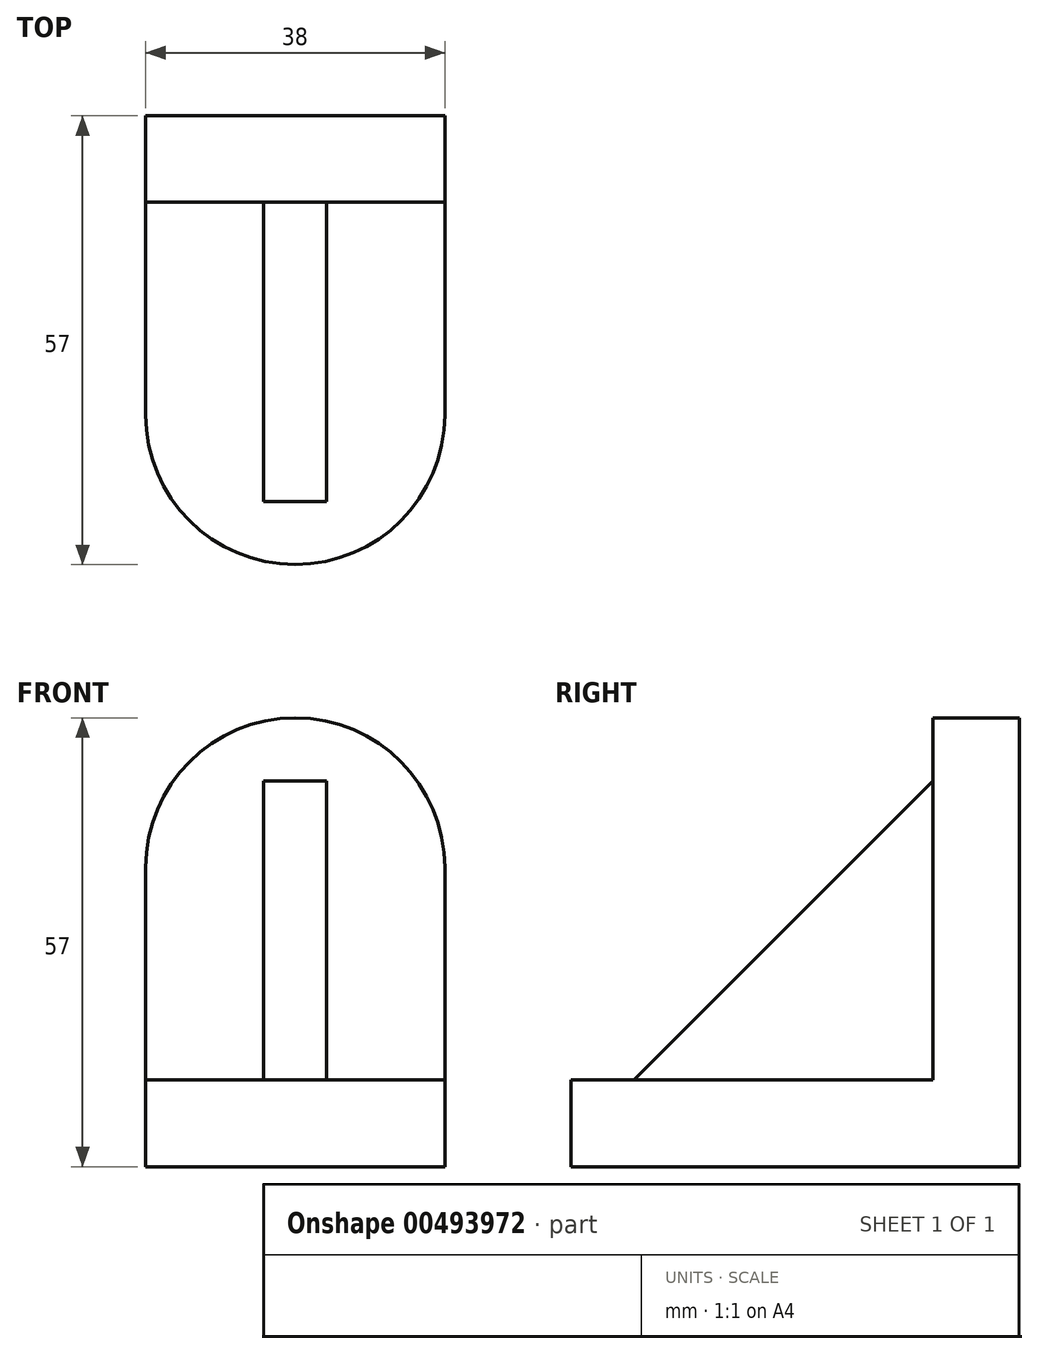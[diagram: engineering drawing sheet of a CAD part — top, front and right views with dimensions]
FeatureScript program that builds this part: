
annotation { "Feature Type Name" : "Feature", "Feature Type Description" : "" }
export const myFeature = defineFeature(function(context is Context, id is Id, definition is map)
    precondition{}
    {
        {
            var Q0;
            Q0=qCreatedBy(makeId("Front.planeOp"),FACE);
            var sketch = newSketch(context, id + "F0", { "sketchPlane" : qUnion([Q0])});
            skLineSegment(sketch, "E0.bottom", {"start": v(-19, 0) * mm, "end": v(19, 0) * mm});
            skLineSegment(sketch, "E0.left", {"start": v(-19, 0) * mm, "end": v(-19, 38) * mm});
            skLineSegment(sketch, "E0.right", {"start": v(19, 0) * mm, "end": v(19, 38) * mm});
            skArc(sketch, "E1", {"start": v(19, 38) * mm, "mid": v(0, 57) * mm, "end": v(-19, 38) * mm});
            skSolve(sketch);
        }
        {
            var Q0;
            Q0=makeQuery(id+"F0.imprint","IMPRINT",FACE,{"disambiguationData":[TD([[makeQuery(id+"F0.imprint","IMPRINT",EDGE,{"derivedFrom":sQuery(id+"F0.wireOp",EDGE,"E0.bottom")}),1.0]])]});
            extrude(context, id + "F1", {"entities" : qUnion([Q0]), "depth" : 11 * mm});
        }
        {
            var Q0;
            Q0=qCreatedBy(makeId("Top.planeOp"),FACE);
            var sketch = newSketch(context, id + "F2", { "sketchPlane" : qUnion([Q0])});
            skLineSegment(sketch, "E2.bottom", {"start": v(-19, 0) * mm, "end": v(19, 0) * mm});
            skLineSegment(sketch, "E2.left", {"start": v(-19, 0) * mm, "end": v(-19, -38) * mm});
            skLineSegment(sketch, "E2.right", {"start": v(19, 0) * mm, "end": v(19, -38) * mm});
            skArc(sketch, "E3", {"start": v(-19, -38) * mm, "mid": v(0, -57) * mm, "end": v(19, -38) * mm});
            skSolve(sketch);
        }
        {
            var Q0;
            Q0=makeQuery(id+"F2.imprint","IMPRINT",FACE,{"disambiguationData":[TD([[makeQuery(id+"F2.imprint","IMPRINT",EDGE,{"derivedFrom":sQuery(id+"F2.wireOp",EDGE,"E2.bottom")}),-1.0]])]});
            extrude(context, id + "F3", {"entities" : qUnion([Q0]), "operationType" : NewBodyOperationType.ADD, "depth" : 11 * mm});
        }
        {
            var Q0;
            Q0=qCreatedBy(makeId("Right.planeOp"),FACE);
            var sketch = newSketch(context, id + "F4", { "sketchPlane" : qUnion([Q0])});
            skLineSegment(sketch, "E4", {"start": v(-49, 11) * mm, "end": v(-11, 49) * mm});
            skLineSegment(sketch, "E5", {"start": v(-11, 49) * mm, "end": v(-11, 9.03) * mm});
            skLineSegment(sketch, "E6", {"start": v(-11, 9.03) * mm, "end": v(-49, 11) * mm});
            skSolve(sketch);
        }
        {
            var Q0;
            Q0=makeQuery(id+"F4.imprint","IMPRINT",FACE,{"disambiguationData":[TD([[makeQuery(id+"F4.imprint","IMPRINT",EDGE,{"derivedFrom":sQuery(id+"F4.wireOp",EDGE,"E4")}),-1.0]])]});
            extrude(context, id + "F5", {"entities" : qUnion([Q0]), "operationType" : NewBodyOperationType.ADD, "depth" : 4 * mm});
        }
        {
            var Q0;
            Q0=makeQuery(id+"F1.opExtrude","SWEPT_BODY",BODY,{"disambiguationData":[OSD([sQuery(id+"F0.wireOp",EDGE,"E0.bottom"),sQuery(id+"F0.wireOp",EDGE,"E0.left"),sQuery(id+"F0.wireOp",EDGE,"E0.right"),sQuery(id+"F0.wireOp",EDGE,"E1")])]});
            var Q1;
            Q1=qCreatedBy(makeId("Right.planeOp"),FACE);
            mirror(context, id + "F6", {"operationType" : NewBodyOperationType.ADD, "entities" : qUnion([Q0]), "mirrorPlane" : qUnion([Q1])});
        }
    });
